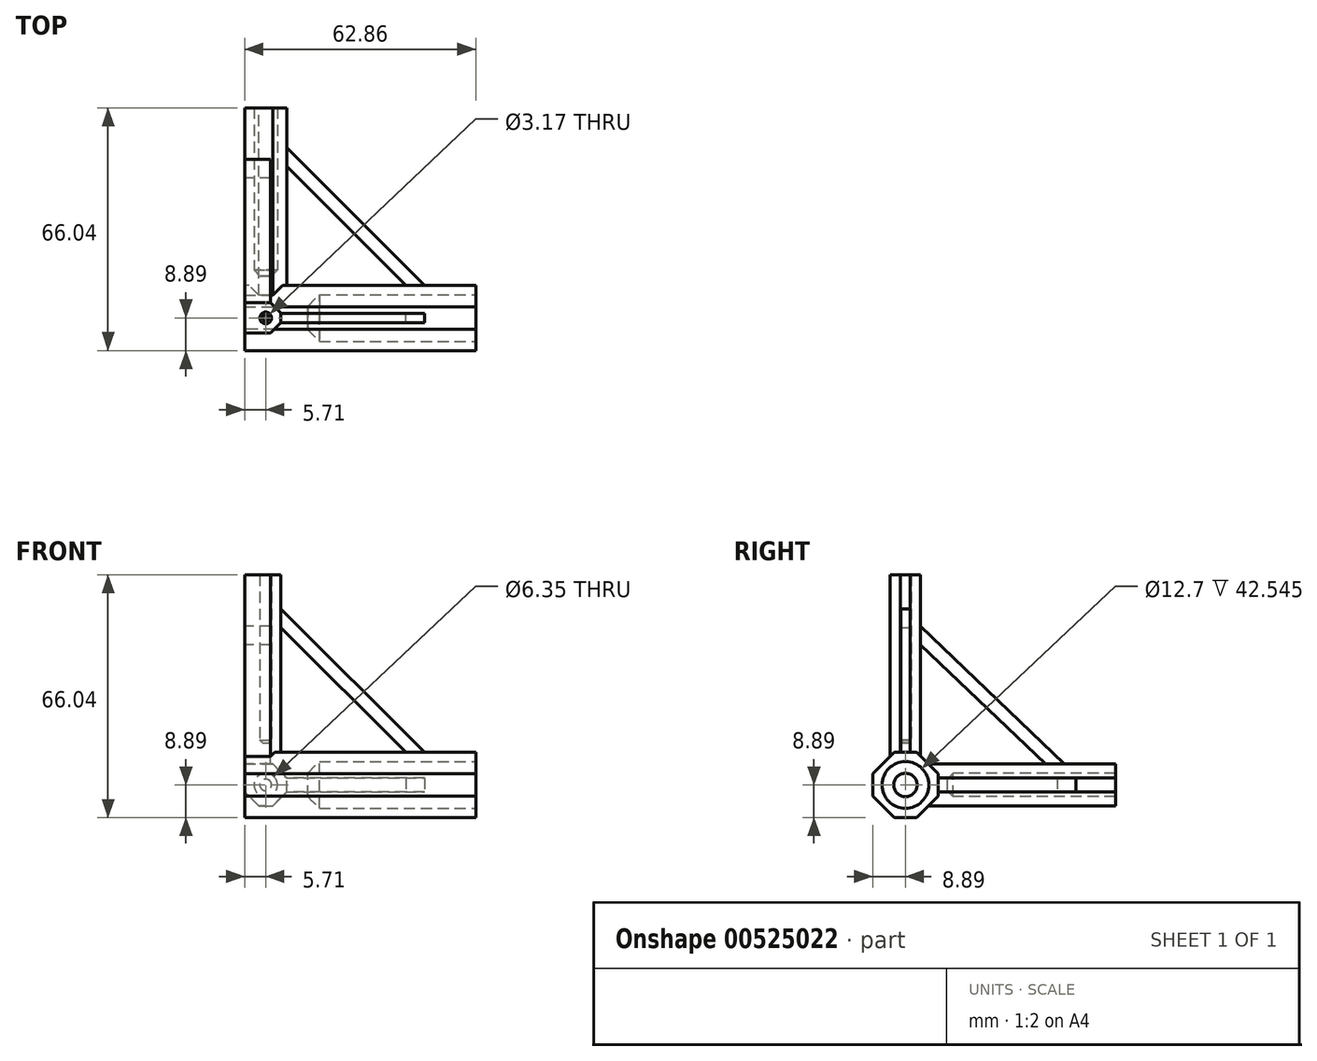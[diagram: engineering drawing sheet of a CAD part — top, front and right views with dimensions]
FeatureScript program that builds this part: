
annotation { "Feature Type Name" : "Feature", "Feature Type Description" : "" }
export const myFeature = defineFeature(function(context is Context, id is Id, definition is map)
    precondition{}
    {
        {
            var Q0;
            Q0=qCreatedBy(makeId("Front.planeOp"),FACE);
            var sketch = newSketch(context, id + "F0", { "sketchPlane" : qUnion([Q0])});
            skLineSegment(sketch, "E0", {"start": v(8.9, 0) * mm, "end": v(8.9, 6.35) * mm, "construction": true});
            skLineSegment(sketch, "E1", {"start": v(8.9, 6.35) * mm, "end": v(8.9, 8.9) * mm, "construction": true});
            skLineSegment(sketch, "E2", {"start": v(8.9, 0) * mm, "end": v(11.43, 0) * mm, "construction": true});
            skLineSegment(sketch, "E3", {"start": v(11.43, 0) * mm, "end": v(11.43, 3.18) * mm});
            skLineSegment(sketch, "E4", {"start": v(14.6, 6.35) * mm, "end": v(62.23, 6.35) * mm});
            skLineSegment(sketch, "E5", {"start": v(62.23, 6.35) * mm, "end": v(62.23, 8.9) * mm, "construction": true});
            skLineSegment(sketch, "E6", {"start": v(62.23, 8.9) * mm, "end": v(8.9, 8.9) * mm, "construction": true});
            skLineSegment(sketch, "E7", {"start": v(11.43, 3.18) * mm, "end": v(14.6, 6.35) * mm});
            skPoint(sketch, "E8.orphan", {"position": v(11.43, 6.35) * mm});
            skLineSegment(sketch, "E9", {"start": v(11.43, 0) * mm, "end": v(62.23, 0) * mm});
            skLineSegment(sketch, "E10", {"start": v(62.23, 6.35) * mm, "end": v(62.23, 0) * mm});
            skSolve(sketch);
        }
        {
            var Q0;
            Q0=qCreatedBy(makeId("Right.planeOp"),FACE);
            var sketch = newSketch(context, id + "F1", { "sketchPlane" : qUnion([Q0])});
            skLineSegment(sketch, "E11.bottom", {"start": v(-8.89, -8.9) * mm, "end": v(8.9, -8.9) * mm});
            skLineSegment(sketch, "E11.top", {"start": v(-8.9, 8.9) * mm, "end": v(8.89, 8.9) * mm});
            skLineSegment(sketch, "E11.left", {"start": v(-8.89, -8.9) * mm, "end": v(-8.9, 8.9) * mm});
            skLineSegment(sketch, "E11.right", {"start": v(8.9, -8.9) * mm, "end": v(8.89, 8.9) * mm});
            skPoint(sketch, "E11.middle", {"position": v(0, 0) * mm});
            skSolve(sketch);
        }
        {
            var Q0;
            Q0=makeQuery(id+"F1.imprint","IMPRINT",FACE,{"disambiguationData":[TD([[makeQuery(id+"F1.imprint","IMPRINT",EDGE,{"derivedFrom":sQuery(id+"F1.wireOp",EDGE,"E11.bottom")}),1.0]])]});
            extrude(context, id + "F2", {"entities" : qUnion([Q0]), "depth" : 57.15 * mm, "offsetDistance" : 25.4 * mm});
        }
        {
            var Q0;
            Q0=qSketchRegion(id+"F0",true);
            var Q1;
            Q1=sQuery(id+"F0.wireOp",EDGE,"E9");
            revolve(context, id + "F3", {"operationType" : NewBodyOperationType.REMOVE, "entities" : qUnion([Q0]), "axis" : qUnion([Q1]), "revolveType" : RevolveType.FULL, "oppositeDirection" : true});
        }
        {
            var Q0;
            Q0=makeQuery(id+"F2.opExtrude","SWEPT_EDGE",EDGE,{"disambiguationData":[OSD([sQuery(id+"F1.wireOp",EDGE,"E11.bottom"),sQuery(id+"F1.wireOp",EDGE,"E11.left")])]});
            var Q1;
            Q1=makeQuery(id+"F2.opExtrude","SWEPT_EDGE",EDGE,{"disambiguationData":[OSD([sQuery(id+"F1.wireOp",EDGE,"E11.top"),sQuery(id+"F1.wireOp",EDGE,"E11.right")])]});
            var Q2;
            Q2=makeQuery(id+"F2.opExtrude","SWEPT_EDGE",EDGE,{"disambiguationData":[OSD([sQuery(id+"F1.wireOp",EDGE,"E11.top"),sQuery(id+"F1.wireOp",EDGE,"E11.left")])]});
            var Q3;
            Q3=makeQuery(id+"F2.opExtrude","SWEPT_EDGE",EDGE,{"disambiguationData":[OSD([sQuery(id+"F1.wireOp",EDGE,"E11.bottom"),sQuery(id+"F1.wireOp",EDGE,"E11.right")])]});
            chamfer(context, id + "F4", {"entities" : qUnion([Q0, Q1, Q2, Q3]), "width" : 5.84 * mm, "tangentPropagation" : true});
        }
        {
            var Q0;
            Q0=qCreatedBy(makeId("Right.planeOp"),FACE);
            var sketch = newSketch(context, id + "F5", { "sketchPlane" : qUnion([Q0])});
            skPoint(sketch, "E12.0", {"position": v(0, 8.9) * mm});
            skLineSegment(sketch, "E13", {"start": v(4.13, 8.9) * mm, "end": v(0, 8.9) * mm, "construction": true});
            skLineSegment(sketch, "E14", {"start": v(0, 8.9) * mm, "end": v(0, 11.43) * mm, "construction": true});
            skLineSegment(sketch, "E15", {"start": v(0, 11.43) * mm, "end": v(0.8, 11.43) * mm});
            skLineSegment(sketch, "E16", {"start": v(1.59, 12.22) * mm, "end": v(1.59, 66.04) * mm});
            skLineSegment(sketch, "E17", {"start": v(1.59, 66.04) * mm, "end": v(4.13, 66.04) * mm, "construction": true});
            skLineSegment(sketch, "E18", {"start": v(4.13, 66.04) * mm, "end": v(4.13, 8.9) * mm, "construction": true});
            skLineSegment(sketch, "E19", {"start": v(0.8, 11.43) * mm, "end": v(1.59, 12.22) * mm});
            skPoint(sketch, "E20.orphan", {"position": v(1.59, 11.43) * mm});
            skPoint(sketch, "E21.endSnap0", {"position": v(0, 10.16) * mm});
            skLineSegment(sketch, "E22", {"start": v(1.59, 66.04) * mm, "end": v(0, 66.04) * mm});
            skLineSegment(sketch, "E23", {"start": v(0, 66.04) * mm, "end": v(0, 11.43) * mm});
            skSolve(sketch);
        }
        {
            var Q0;
            Q0=qCreatedBy(makeId("Top.planeOp"),FACE);
            var sketch = newSketch(context, id + "F6", { "sketchPlane" : qUnion([Q0])});
            skLineSegment(sketch, "E24.bottom", {"start": v(-4.13, -4.13) * mm, "end": v(4.13, -4.13) * mm});
            skLineSegment(sketch, "E24.top", {"start": v(-4.13, 4.13) * mm, "end": v(4.13, 4.13) * mm});
            skLineSegment(sketch, "E24.left", {"start": v(-4.13, -4.13) * mm, "end": v(-4.13, 4.13) * mm});
            skLineSegment(sketch, "E24.right", {"start": v(4.13, -4.13) * mm, "end": v(4.13, 4.13) * mm});
            skPoint(sketch, "E24.middle", {"position": v(0, 0) * mm});
            skLineSegment(sketch, "E25", {"start": v(-4.13, -4.13) * mm, "end": v(-6.67, -4.13) * mm});
            skLineSegment(sketch, "E26", {"start": v(-6.67, -4.13) * mm, "end": v(-6.67, 4.05) * mm});
            skLineSegment(sketch, "E27", {"start": v(-6.67, 4.05) * mm, "end": v(-4.13, 4.13) * mm});
            skSolve(sketch);
        }
        {
            var Q0;
            Q0=makeQuery(id+"F6.imprint","IMPRINT",FACE,{"disambiguationData":[TD([[makeQuery(id+"F6.imprint","IMPRINT",EDGE,{"derivedFrom":sQuery(id+"F6.wireOp",EDGE,"E24.bottom")}),1.0]])]});
            extrude(context, id + "F7", {"entities" : qUnion([Q0]), "depth" : 57.15 * mm, "offsetDistance" : 25.4 * mm});
        }
        {
            var Q0;
            Q0=makeQuery(id+"F7.opExtrude","CAP_FACE",FACE,{"disambiguationData":[OSD([sQuery(id+"F6.wireOp",EDGE,"E24.bottom"),sQuery(id+"F6.wireOp",EDGE,"E24.top"),sQuery(id+"F6.wireOp",EDGE,"E24.left"),sQuery(id+"F6.wireOp",EDGE,"E24.right")])],"isStart":true});
            var Q1;
            Q1=makeQuery(id+"F2.opExtrude","SWEPT_FACE",FACE,{"disambiguationData":[OSD([sQuery(id+"F1.wireOp",EDGE,"E11.bottom")])]});
            extrude(context, id + "F8", {"entities" : qUnion([Q0]), "operationType" : NewBodyOperationType.ADD, "endBound" : BoundingType.UP_TO_SURFACE, "depth" : 25.4 * mm, "endBoundEntityFace" : qUnion([Q1]), "offsetDistance" : 25.4 * mm});
        }
        {
            var Q0;
            Q0=qSketchRegion(id+"F5",true);
            var Q1;
            Q1=sQuery(id+"F5.wireOp",EDGE,"E23");
            revolve(context, id + "F9", {"operationType" : NewBodyOperationType.REMOVE, "entities" : qUnion([Q0]), "axis" : qUnion([Q1]), "revolveType" : RevolveType.FULL, "oppositeDirection" : true});
        }
        {
            var Q0;
            {var subQ0=sQuery(id+"F6.wireOp",EDGE,"E24.right");var subQ1=sQuery(id+"F6.wireOp",EDGE,"E24.top");Q0=makeQuery(id+"F8.boolean.opBoolean","MERGE",EDGE,{"derivedFrom":[makeQuery(id+"F7.opExtrude","SWEPT_EDGE",EDGE,{"disambiguationData":[OSD([subQ1,subQ0])]}),makeQuery(id+"F8.opExtrude","SWEPT_EDGE",EDGE,{"disambiguationData":[OSD([subQ1,subQ0])]})]});}
            var Q1;
            {var subQ0=sQuery(id+"F6.wireOp",EDGE,"E24.right");var subQ1=sQuery(id+"F6.wireOp",EDGE,"E24.bottom");Q1=makeQuery(id+"F8.boolean.opBoolean","MERGE",EDGE,{"derivedFrom":[makeQuery(id+"F7.opExtrude","SWEPT_EDGE",EDGE,{"disambiguationData":[OSD([subQ1,subQ0])]}),makeQuery(id+"F8.opExtrude","SWEPT_EDGE",EDGE,{"disambiguationData":[OSD([subQ1,subQ0])]})]});}
            chamfer(context, id + "F10", {"entities" : qUnion([Q0, Q1]), "width" : 2.8 * mm, "tangentPropagation" : true});
        }
        {
            var Q0;
            Q0=qCreatedBy(makeId("Top.planeOp"),FACE);
            var sketch = newSketch(context, id + "F11", { "sketchPlane" : qUnion([Q0])});
            skLineSegment(sketch, "E28", {"start": v(0, 8.9) * mm, "end": v(-5.72, 8.9) * mm, "construction": true});
            skLineSegment(sketch, "E29", {"start": v(-5.72, 8.9) * mm, "end": v(-5.72, 66.04) * mm, "construction": true});
            skLineSegment(sketch, "E30", {"start": v(-5.72, 66.04) * mm, "end": v(-3.18, 66.04) * mm, "construction": true});
            skLineSegment(sketch, "E31", {"start": v(-3.17, 66.04) * mm, "end": v(-3.17, 13.02) * mm});
            skLineSegment(sketch, "E32", {"start": v(-1.59, 11.43) * mm, "end": v(0, 11.43) * mm});
            skLineSegment(sketch, "E33", {"start": v(0, 11.43) * mm, "end": v(-1.59, 11.43) * mm});
            skLineSegment(sketch, "E34", {"start": v(-1.59, 11.43) * mm, "end": v(-3.18, 13.02) * mm});
            skPoint(sketch, "E35.orphan", {"position": v(-3.17, 11.43) * mm});
            skLineSegment(sketch, "E36", {"start": v(0, 11.43) * mm, "end": v(0, 8.89) * mm, "construction": true});
            skLineSegment(sketch, "E37", {"start": v(0, 11.43) * mm, "end": v(0, 37.76) * mm, "construction": true});
            skLineSegment(sketch, "E38", {"start": v(0, 11.43) * mm, "end": v(0, 66.04) * mm});
            skLineSegment(sketch, "E39", {"start": v(0, 66.04) * mm, "end": v(-3.17, 66.04) * mm});
            skSolve(sketch);
        }
        {
            var Q0;
            Q0=qCreatedBy(makeId("Front.planeOp"),FACE);
            var sketch = newSketch(context, id + "F12", { "sketchPlane" : qUnion([Q0])});
            skLineSegment(sketch, "E40.bottom", {"start": v(-5.71, -5.72) * mm, "end": v(5.72, -5.72) * mm});
            skLineSegment(sketch, "E40.top", {"start": v(-5.72, 5.72) * mm, "end": v(5.71, 5.72) * mm});
            skLineSegment(sketch, "E40.left", {"start": v(-5.71, -5.72) * mm, "end": v(-5.72, 5.72) * mm});
            skLineSegment(sketch, "E40.right", {"start": v(5.72, -5.72) * mm, "end": v(5.71, 5.72) * mm});
            skPoint(sketch, "E40.middle", {"position": v(0, 0) * mm});
            skSolve(sketch);
        }
        {
            var Q0;
            Q0=qSketchRegion(id+"F12",true);
            extrude(context, id + "F13", {"entities" : qUnion([Q0]), "oppositeDirection" : true, "depth" : 57.15 * mm, "offsetDistance" : 25.4 * mm});
        }
        {
            var Q0;
            Q0=qSketchRegion(id+"F11",true);
            var Q1;
            Q1=sQuery(id+"F11.wireOp",EDGE,"E37");
            revolve(context, id + "F14", {"operationType" : NewBodyOperationType.REMOVE, "entities" : qUnion([Q0]), "axis" : qUnion([Q1]), "revolveType" : RevolveType.FULL});
        }
        {
            var Q0;
            Q0=makeQuery(id+"F13.opExtrude","SWEPT_EDGE",EDGE,{"disambiguationData":[OSD([sQuery(id+"F12.wireOp",EDGE,"E40.top"),sQuery(id+"F12.wireOp",EDGE,"E40.right")])]});
            var Q1;
            Q1=makeQuery(id+"F13.opExtrude","SWEPT_EDGE",EDGE,{"disambiguationData":[OSD([sQuery(id+"F12.wireOp",EDGE,"E40.bottom"),sQuery(id+"F12.wireOp",EDGE,"E40.right")])]});
            var Q2;
            Q2=makeQuery(id+"F13.opExtrude","SWEPT_EDGE",EDGE,{"disambiguationData":[OSD([sQuery(id+"F12.wireOp",EDGE,"E40.bottom"),sQuery(id+"F12.wireOp",EDGE,"E40.left")])]});
            chamfer(context, id + "F15", {"entities" : qUnion([Q0, Q1, Q2]), "width" : 3.8 * mm, "tangentPropagation" : true});
        }
        {
            var Q0;
            Q0=qCreatedBy(makeId("Front.planeOp"),FACE);
            var sketch = newSketch(context, id + "F16", { "sketchPlane" : qUnion([Q0])});
            skLineSegment(sketch, "E41.0", {"start": v(4.13, 57.15) * mm, "end": v(4.13, -8.9) * mm, "construction": true});
            skLineSegment(sketch, "E42", {"start": v(4.13, 47.94) * mm, "end": v(43.18, 8.89) * mm});
            skLineSegment(sketch, "E43", {"start": v(4.13, 47.94) * mm, "end": v(4.13, 42.86) * mm, "construction": true});
            skLineSegment(sketch, "E44", {"start": v(43.18, 8.89) * mm, "end": v(38.1, 8.9) * mm});
            skLineSegment(sketch, "E45", {"start": v(38.1, 8.9) * mm, "end": v(43.18, 8.89) * mm, "construction": true});
            skLineSegment(sketch, "E46", {"start": v(4.13, 42.86) * mm, "end": v(38.1, 8.9) * mm});
            skLineSegment(sketch, "E47", {"start": v(4.13, 47.94) * mm, "end": v(4.13, 42.86) * mm});
            skSolve(sketch);
        }
        {
            var Q0;
            Q0=makeQuery(id+"F16.imprint","IMPRINT",FACE,{"disambiguationData":[TD([[makeQuery(id+"F16.imprint","IMPRINT",EDGE,{"derivedFrom":sQuery(id+"F16.wireOp",EDGE,"E42")}),-1.0]])]});
            extrude(context, id + "F17", {"entities" : qUnion([Q0]), "operationType" : NewBodyOperationType.ADD, "depth" : 2.54 * mm, "offsetDistance" : 25.4 * mm, "symmetric" : true});
        }
        {
            var Q0;
            Q0=qCreatedBy(makeId("Top.planeOp"),FACE);
            var sketch = newSketch(context, id + "F18", { "sketchPlane" : qUnion([Q0])});
            skLineSegment(sketch, "E48", {"start": v(5.71, 46.36) * mm, "end": v(43.18, 8.89) * mm});
            skLineSegment(sketch, "E49", {"start": v(43.18, 8.9) * mm, "end": v(38.1, 8.89) * mm});
            skLineSegment(sketch, "E50", {"start": v(38.1, 8.89) * mm, "end": v(5.71, 41.28) * mm});
            skLineSegment(sketch, "E51", {"start": v(5.72, 41.27) * mm, "end": v(5.72, 46.35) * mm});
            skSolve(sketch);
        }
        {
            var Q0;
            Q0=makeQuery(id+"F18.imprint","IMPRINT",FACE,{"disambiguationData":[TD([[makeQuery(id+"F18.imprint","IMPRINT",EDGE,{"derivedFrom":sQuery(id+"F18.wireOp",EDGE,"E48")}),-1.0]])]});
            extrude(context, id + "F19", {"entities" : qUnion([Q0]), "operationType" : NewBodyOperationType.ADD, "depth" : 3.8 * mm, "offsetDistance" : 25.4 * mm, "symmetric" : true});
        }
        {
            var Q0;
            Q0=makeQuery(id+"F1.imprint","IMPRINT",FACE,{"disambiguationData":[TD([[makeQuery(id+"F1.imprint","IMPRINT",EDGE,{"derivedFrom":sQuery(id+"F1.wireOp",EDGE,"E11.bottom")}),1.0]])]});
            var Q1;
            Q1=makeQuery(id+"F13.opExtrude","SWEPT_FACE",FACE,{"disambiguationData":[OSD([sQuery(id+"F12.wireOp",EDGE,"E40.left")])]});
            extrude(context, id + "F20", {"entities" : qUnion([Q0]), "operationType" : NewBodyOperationType.ADD, "endBound" : BoundingType.UP_TO_SURFACE, "oppositeDirection" : true, "depth" : 25.4 * mm, "endBoundEntityFace" : qUnion([Q1]), "offsetDistance" : 25.4 * mm});
        }
        {
            var Q0;
            Q0=makeQuery(id+"F20.opExtrude","SWEPT_EDGE",EDGE,{"disambiguationData":[OSD([sQuery(id+"F1.wireOp",EDGE,"E11.top"),sQuery(id+"F1.wireOp",EDGE,"E11.right")])]});
            var Q1;
            Q1=makeQuery(id+"F20.opExtrude","SWEPT_EDGE",EDGE,{"disambiguationData":[OSD([sQuery(id+"F1.wireOp",EDGE,"E11.top"),sQuery(id+"F1.wireOp",EDGE,"E11.left")])]});
            var Q2;
            Q2=makeQuery(id+"F20.opExtrude","SWEPT_EDGE",EDGE,{"disambiguationData":[OSD([sQuery(id+"F1.wireOp",EDGE,"E11.bottom"),sQuery(id+"F1.wireOp",EDGE,"E11.left")])]});
            var Q3;
            Q3=makeQuery(id+"F20.opExtrude","SWEPT_EDGE",EDGE,{"disambiguationData":[OSD([sQuery(id+"F1.wireOp",EDGE,"E11.bottom"),sQuery(id+"F1.wireOp",EDGE,"E11.right")])]});
            chamfer(context, id + "F21", {"entities" : qUnion([Q0, Q1, Q2, Q3]), "width" : 5.84 * mm, "tangentPropagation" : true});
        }
        {
            var Q0;
            {var subQ0=sQuery(id+"F6.wireOp",EDGE,"E24.left");Q0=makeQuery(id+"F8.boolean.opBoolean","MERGE",FACE,{"derivedFrom":[makeQuery(id+"F7.opExtrude","SWEPT_FACE",FACE,{"disambiguationData":[OSD([subQ0])]}),makeQuery(id+"F8.opExtrude","SWEPT_FACE",FACE,{"disambiguationData":[OSD([subQ0])]})]});}
            var Q1;
            {var subQ0=sQuery(id+"F12.wireOp",EDGE,"E40.left");Q1=makeQuery(id+"F20.boolean.opBoolean","MERGE",FACE,{"derivedFrom":[makeQuery(id+"F13.opExtrude","SWEPT_FACE",FACE,{"disambiguationData":[OSD([subQ0])]}),makeQuery(id+"F20.opExtrude","CAP_FACE",FACE,{"disambiguationData":[OSD([subQ0])],"isStart":false})]});}
            extrude(context, id + "F22", {"entities" : qUnion([Q0]), "operationType" : NewBodyOperationType.ADD, "endBound" : BoundingType.UP_TO_SURFACE, "depth" : 25.4 * mm, "endBoundEntityFace" : qUnion([Q1]), "offsetDistance" : 25.4 * mm});
        }
        {
            var Q0;
            {var subQ0=sQuery(id+"F12.wireOp",EDGE,"E40.left");Q0=makeQuery(id+"F22.boolean.opBoolean","MERGE",FACE,{"derivedFrom":[makeQuery(id+"F20.boolean.opBoolean","MERGE",FACE,{"derivedFrom":[makeQuery(id+"F13.opExtrude","SWEPT_FACE",FACE,{"disambiguationData":[OSD([subQ0])]}),makeQuery(id+"F20.opExtrude","CAP_FACE",FACE,{"disambiguationData":[OSD([subQ0])],"isStart":false})]}),makeQuery(id+"F22.opExtrude","CAP_FACE",FACE,{"disambiguationData":[OSD([subQ0])],"isStart":false})]});}
            cPlane(context, id + "F23", {"entities" : qUnion([Q0]), "cplaneType" : CPlaneType.OFFSET, "offset" : 0 * mm, "oppositeDirection" : true, "width" : 152.4 * mm, "height" : 152.4 * mm});
        }
        {
            var Q0;
            Q0=qCreatedBy(id+"F23.planeOp",FACE);
            var sketch = newSketch(context, id + "F24", { "sketchPlane" : qUnion([Q0])});
            skLineSegment(sketch, "E52.0", {"start": v(-4.13, 66.04) * mm, "end": v(-4.13, 8.9) * mm, "construction": true});
            skLineSegment(sketch, "E53.0", {"start": v(-6.22, 5.71) * mm, "end": v(-57.15, 5.71) * mm});
            skLineSegment(sketch, "E54", {"start": v(-43.18, 5.71) * mm, "end": v(-4.13, 43.18) * mm});
            skLineSegment(sketch, "E55", {"start": v(-4.13, 43.18) * mm, "end": v(-4.13, 38.1) * mm});
            skLineSegment(sketch, "E56", {"start": v(-4.13, 38.1) * mm, "end": v(-38.1, 5.71) * mm});
            skLineSegment(sketch, "E57", {"start": v(-38.1, 5.71) * mm, "end": v(-43.18, 5.71) * mm});
            skSolve(sketch);
        }
        {
            var Q0;
            Q0 = qSketchRegion(id + "F24", true);
            var Q1;
            {var subQ0=sQuery(id+"F6.wireOp",EDGE,"E24.right");var subQ1=sQuery(id+"F6.wireOp",EDGE,"E24.top");Q1=makeQuery(id+"F10.opChamfer","BLEND_VERTEX",VERTEX,{"blendedFrom":[makeQuery(id+"F8.boolean.opBoolean","MERGE",EDGE,{"derivedFrom":[makeQuery(id+"F7.opExtrude","SWEPT_EDGE",EDGE,{"disambiguationData":[OSD([subQ1,subQ0])]}),makeQuery(id+"F8.opExtrude","SWEPT_EDGE",EDGE,{"disambiguationData":[OSD([subQ1,subQ0])]})]}),makeQuery(id+"F8.boolean.opBoolean","MERGE",FACE,{"derivedFrom":[makeQuery(id+"F7.opExtrude","SWEPT_FACE",FACE,{"disambiguationData":[OSD([subQ1])]}),makeQuery(id+"F8.opExtrude","SWEPT_FACE",FACE,{"disambiguationData":[OSD([subQ1])]})]}),makeQuery(id+"F7.opExtrude","CAP_FACE",FACE,{"disambiguationData":[OSD([sQuery(id+"F6.wireOp",EDGE,"E24.bottom"),subQ1,sQuery(id+"F6.wireOp",EDGE,"E24.left"),subQ0])],"isStart":false})],"blendedInto":[makeQuery(id+"F8.boolean.opBoolean","MERGE",FACE,{"derivedFrom":[makeQuery(id+"F7.opExtrude","SWEPT_FACE",FACE,{"disambiguationData":[OSD([subQ1])]}),makeQuery(id+"F8.opExtrude","SWEPT_FACE",FACE,{"disambiguationData":[OSD([subQ1])]})]}),makeQuery(id+"F7.opExtrude","CAP_FACE",FACE,{"disambiguationData":[OSD([sQuery(id+"F6.wireOp",EDGE,"E24.bottom"),subQ1,sQuery(id+"F6.wireOp",EDGE,"E24.left"),subQ0])],"isStart":false})]});}
            extrude(context, id + "F25", {"entities" : qUnion([Q0]), "operationType" : NewBodyOperationType.ADD, "endBound" : BoundingType.UP_TO_VERTEX, "oppositeDirection" : true, "depth" : 25.4 * mm, "endBoundEntityVertex" : qUnion([Q1]), "offsetDistance" : 25.4 * mm});
        }
    });
